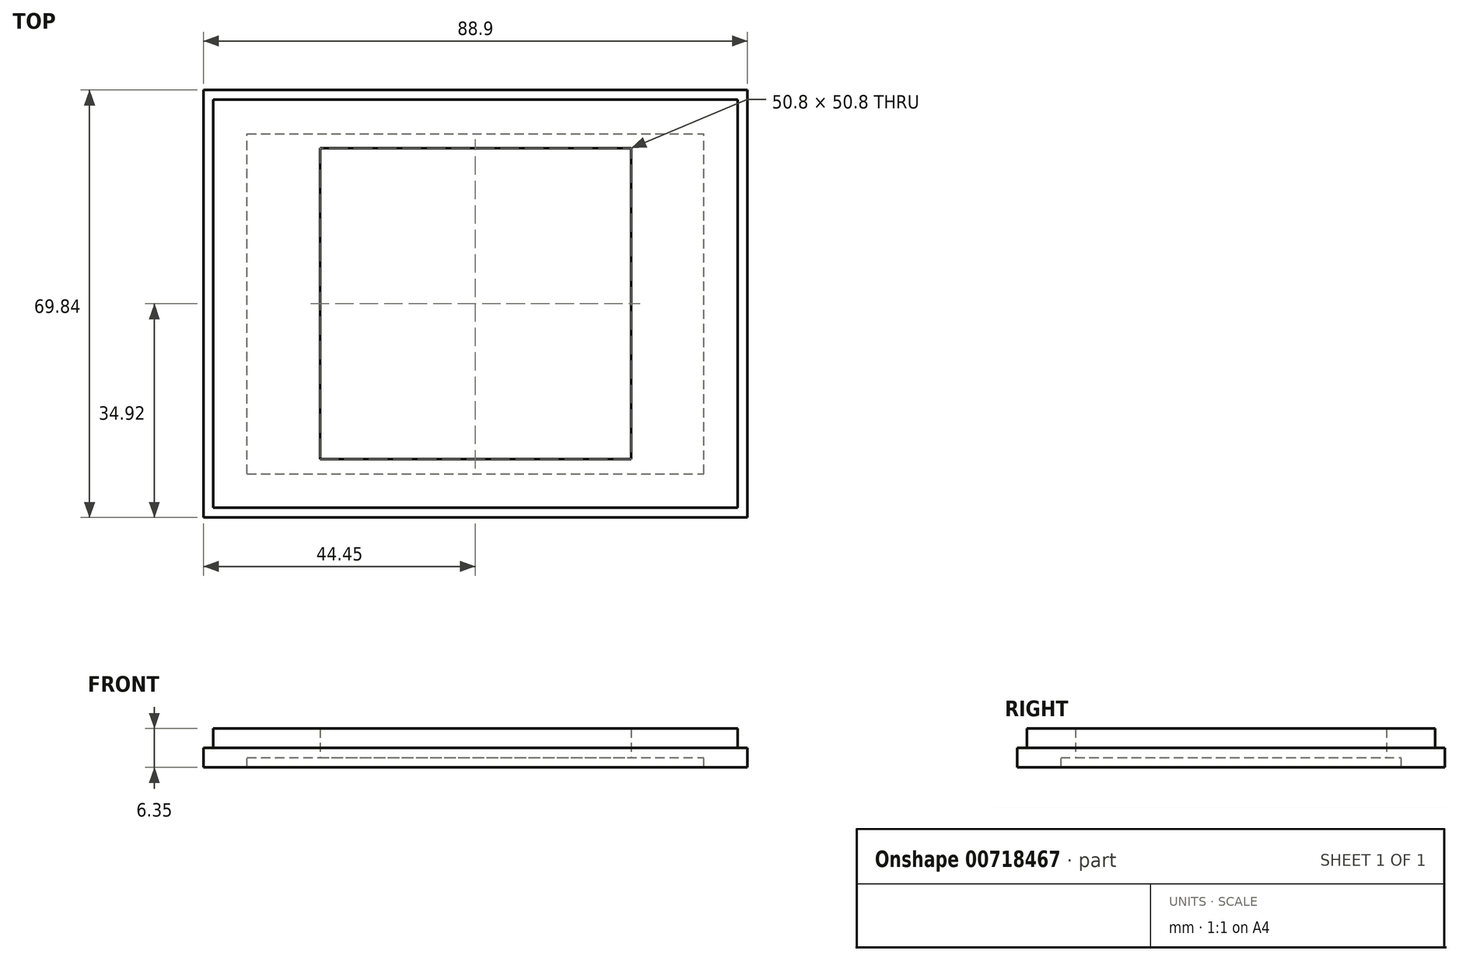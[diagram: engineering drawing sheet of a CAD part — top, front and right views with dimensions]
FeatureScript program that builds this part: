
annotation { "Feature Type Name" : "Feature", "Feature Type Description" : "" }
export const myFeature = defineFeature(function(context is Context, id is Id, definition is map)
    precondition{}
    {
        {
            var Q0;
            Q0=qCreatedBy(makeId("Top.planeOp"),FACE);
            var sketch = newSketch(context, id + "F0", { "sketchPlane" : qUnion([Q0])});
            skLineSegment(sketch, "E0.bottom", {"start": v(-44.45, -34.93) * mm, "end": v(44.45, -34.93) * mm});
            skLineSegment(sketch, "E0.top", {"start": v(-44.45, 34.93) * mm, "end": v(44.45, 34.93) * mm});
            skLineSegment(sketch, "E0.left", {"start": v(-44.45, -34.93) * mm, "end": v(-44.45, 34.93) * mm});
            skLineSegment(sketch, "E0.right", {"start": v(44.45, -34.93) * mm, "end": v(44.45, 34.93) * mm});
            skPoint(sketch, "E0.middle", {"position": v(0, 0) * mm});
            skLineSegment(sketch, "E1.bottom", {"start": v(-42.86, -33.34) * mm, "end": v(42.86, -33.34) * mm});
            skLineSegment(sketch, "E1.top", {"start": v(-42.86, 33.34) * mm, "end": v(42.86, 33.34) * mm});
            skLineSegment(sketch, "E1.left", {"start": v(-42.86, -33.34) * mm, "end": v(-42.86, 33.34) * mm});
            skLineSegment(sketch, "E1.right", {"start": v(42.86, -33.34) * mm, "end": v(42.86, 33.34) * mm});
            skLineSegment(sketch, "E2.bottom", {"start": v(-25.4, -25.4) * mm, "end": v(25.4, -25.4) * mm});
            skLineSegment(sketch, "E2.top", {"start": v(-25.4, 25.4) * mm, "end": v(25.4, 25.4) * mm});
            skLineSegment(sketch, "E2.left", {"start": v(-25.4, -25.4) * mm, "end": v(-25.4, 25.4) * mm});
            skLineSegment(sketch, "E2.right", {"start": v(25.4, -25.4) * mm, "end": v(25.4, 25.4) * mm});
            skLineSegment(sketch, "E3.bottom", {"start": v(-37.3, -27.78) * mm, "end": v(37.3, -27.78) * mm});
            skLineSegment(sketch, "E3.top", {"start": v(-37.3, 27.78) * mm, "end": v(37.3, 27.78) * mm});
            skLineSegment(sketch, "E3.left", {"start": v(-37.3, -27.78) * mm, "end": v(-37.3, 27.78) * mm});
            skLineSegment(sketch, "E3.right", {"start": v(37.3, -27.78) * mm, "end": v(37.3, 27.78) * mm});
            skSolve(sketch);
        }
        {
            var Q0;
            Q0=makeQuery(id+"F0.imprint","IMPRINT",FACE,{"disambiguationData":[TD([[makeQuery(id+"F0.imprint","IMPRINT",EDGE,{"derivedFrom":sQuery(id+"F0.wireOp",EDGE,"E0.bottom")}),1.0]])]});
            extrude(context, id + "F1", {"entities" : qUnion([Q0]), "depth" : 3.17 * mm, "offsetDistance" : 25.4 * mm});
        }
        {
            var Q0;
            Q0=makeQuery(id+"F0.imprint","IMPRINT",FACE,{"disambiguationData":[TD([[makeQuery(id+"F0.imprint","IMPRINT",EDGE,{"derivedFrom":sQuery(id+"F0.wireOp",EDGE,"E1.bottom")}),1.0]])]});
            extrude(context, id + "F2", {"entities" : qUnion([Q0]), "operationType" : NewBodyOperationType.ADD, "depth" : 6.35 * mm, "offsetDistance" : 25.4 * mm});
        }
        {
            var Q0;
            Q0=makeQuery(id+"F0.imprint","IMPRINT",FACE,{"disambiguationData":[TD([[makeQuery(id+"F0.imprint","IMPRINT",EDGE,{"derivedFrom":sQuery(id+"F0.wireOp",EDGE,"E2.bottom")}),-1.0]])]});
            extrude(context, id + "F3", {"entities" : qUnion([Q0]), "operationType" : NewBodyOperationType.ADD, "depth" : 6.35 * mm, "offsetDistance" : 25.4 * mm});
        }
        {
            var Q0;
            Q0=makeQuery(id+"F0.imprint","IMPRINT",FACE,{"disambiguationData":[TD([[makeQuery(id+"F0.imprint","IMPRINT",EDGE,{"derivedFrom":sQuery(id+"F0.wireOp",EDGE,"E2.bottom")}),-1.0]])]});
            extrude(context, id + "F4", {"entities" : qUnion([Q0]), "operationType" : NewBodyOperationType.REMOVE, "endBound" : BoundingType.SYMMETRIC, "oppositeDirection" : true, "depth" : 3.17 * mm, "offsetDistance" : 25.4 * mm});
        }
    });
